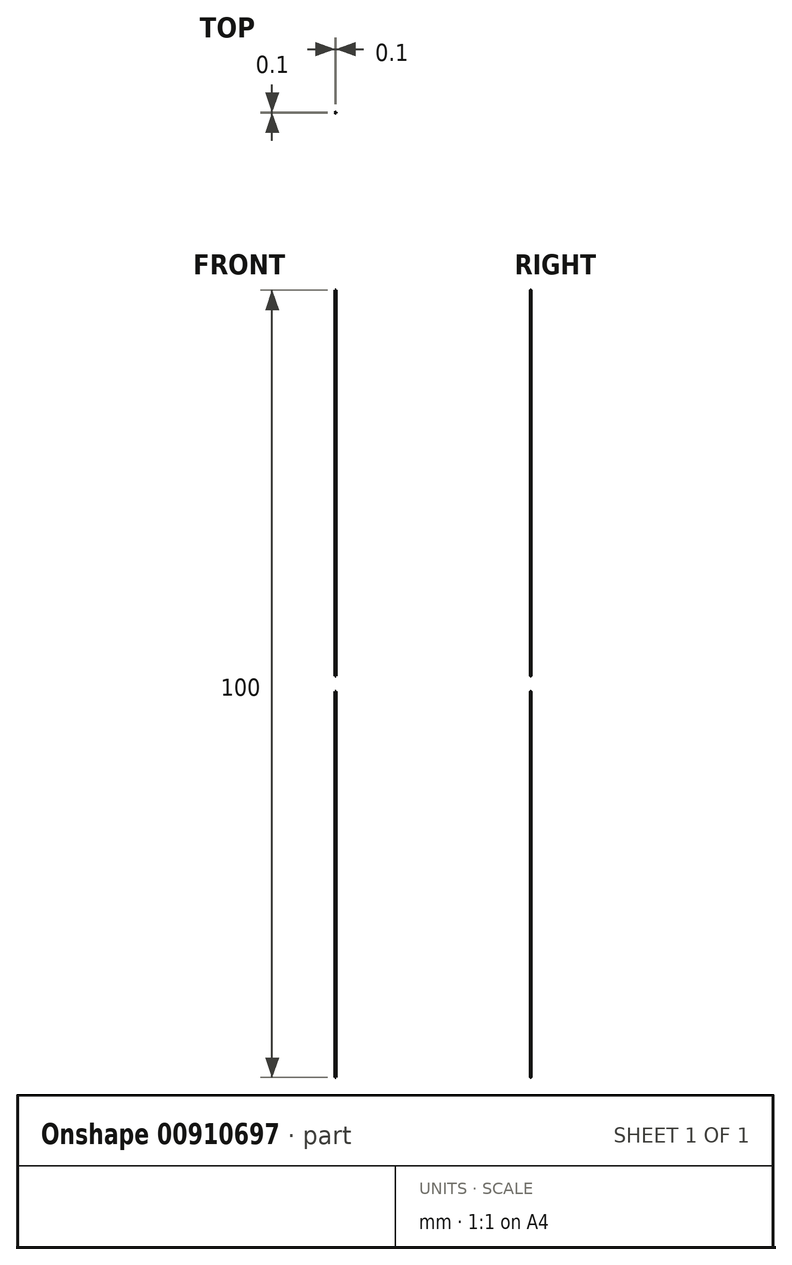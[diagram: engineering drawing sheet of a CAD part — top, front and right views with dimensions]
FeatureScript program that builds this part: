
annotation { "Feature Type Name" : "Feature", "Feature Type Description" : "" }
export const myFeature = defineFeature(function(context is Context, id is Id, definition is map)
    precondition{}
    {
        {
            var Q0;
            Q0=qCreatedBy(makeId("Top.planeOp"),FACE);
            var sketch = newSketch(context, id + "F0", { "sketchPlane" : qUnion([Q0])});
            skCircle(sketch, "E0", {"center": v(0, 0) * mm, "radius": 0.05 * mm});
            skSolve(sketch);
        }
        {
            var Q0;
            Q0=makeQuery(id+"F0.imprint","IMPRINT",FACE,{"disambiguationData":[TD([[makeQuery(id+"F0.imprint","IMPRINT",EDGE,{"derivedFrom":sQuery(id+"F0.wireOp",EDGE,"E0")}),1.0]])]});
            extrude(context, id + "F1", {"entities" : qUnion([Q0]), "depth" : 50 * mm, "offsetDistance" : 25 * mm, "hasSecondDirection" : true, "secondDirectionOppositeDirection" : false, "secondDirectionDepth" : 1 * mm});
        }
        {
            var Q0;
            Q0=makeQuery(id+"F1.opExtrude","SWEPT_BODY",BODY,{"disambiguationData":[OSD([sQuery(id+"F0.wireOp",EDGE,"E0")])]});
            var Q1;
            Q1=qCreatedBy(makeId("Top.planeOp"),FACE);
            mirror(context, id + "F2", {"entities" : qUnion([Q0]), "mirrorPlane" : qUnion([Q1])});
        }
    });
